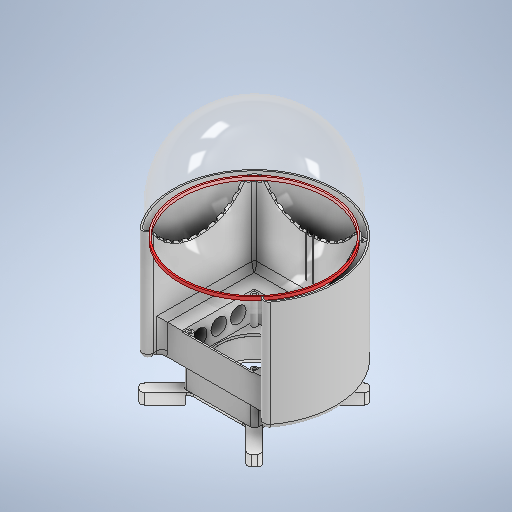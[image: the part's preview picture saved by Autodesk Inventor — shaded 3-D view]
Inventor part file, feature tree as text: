
AUTODESK INVENTOR PART (.ipt)
format: ipt  version: 2025.3 (Build 293356000, 356)  size: 2,002,944 bytes
history: native  units: in
note: dims shown in document units (in); Inventor stores cm internally (conversion verified against a paired STEP export)
features: projected_geometry x27, extrude x22, sketch x21, fillet x10, other x9, pattern_circular x3, mirror x1, helix x1
ambient origin geometry x8: Origin, YZ Plane, XZ Plane, XY Plane, X Axis, Y Axis, Z Axis, Center Point
bodies: Body1 (feature_tree), Body2 (feature_tree), Body3 (feature_tree), Body4 (feature_tree), Body5 (feature_tree), Body6 (feature_tree)
feature tree (94):
  other  "Fan"
  extrude  "Fan Body"  Depth=3.248in
  fillet  "Fillet1"  Radius=0.1772in
  other  "PCB Plane"
  extrude  "PCB extrusion"  Depth=0.1772in
  other  "Bottom of the Coil Plane"
  extrude  "Coil extrusion"  Depth=3.5039in
  sketch  "Sketch5"  dims[d13=0.063in d14=0.0in d15=3.937in]
  other  "Globe revolution"
  extrude  "Inner Wall"  Depth=0.1969in
  sketch  "Sketch7"  dims[d18=0.1575in d19=0.0in d20=7.874in]
  extrude  "Coil Support"  Depth=3.5433in
  extrude  "Coil Support Outer Wall"  Depth=3.937in
  sketch  "Sketch8"  dims[d21=0.0591in d22=90.0deg]
  extrude  "Coil Support Extension"  Depth=0.0787in
  extrude  "Outer Wall"  Depth=7.874in
  extrude  "Extend Walls Bottom of PCB"  TaperAngle=90.0deg  [1 undecoded]
  sketch  "Sketch11"  dims[d27=0.0787in d28=0.0787in d29=0.0in]
  extrude  "Extend Walls to Fan"  Depth=0.1575in TaperAngle=0.0deg
  sketch  "Sketch12"  dims[d30=0.0787in d31=0.0in d34=0.3937in d35=0.0in]
  extrude  "PCB Supports"  Depth=0.0787in TaperAngle=0.0deg
  extrude  "Floor"  Depth=0.3937in TaperAngle=0.0deg
  sketch  "Sketch13"  dims[d36=0.3937in d37=0.0in d40=0.3937in d41=0.0in]
  extrude  "Air Holes"  Depth=0.3937in TaperAngle=0.0deg
  pattern_circular  "Pattern Air Holes"  Count=2  [1 undecoded]
  other  "Cutout Globe"
  extrude  "Cutout Overhang of Coil Support"  Depth=0.7874in
  sketch  "Sketch15"  dims[d50=0.3937in d51=0.0in]
  extrude  "Crown Air Holes"  Depth=0.1181in TaperAngle=0.0deg
  pattern_circular  "Pattern Crown Air Holes"  Count=3  [1 undecoded]
  extrude  "Coil Slots"  Depth=0.3937in TaperAngle=0.0deg
  sketch  "Sketch19"  dims[d62=0.9843in d63=0.1181in d64=0.0in d65=1.1811in d66=-1.2368in]
  sketch  "Sketch20"  dims[d70=90.0deg d71=0.3937in d72=0.0in]
  extrude  "Fill in PCB void"  Depth=0.4331in
  extrude  "PCB Lip"  Depth=3.937in
  extrude  "Repair Fan Air Holes"  Depth=0.1969in TaperAngle=0.0deg
  pattern_circular  "Pattern Repair Air Holes"  Count=3 Angle=180.0deg
  extrude  "Feet Fan Base"  Depth=0.3937in TaperAngle=0.0deg
  extrude  "Feet"  Depth=0.1969in
  mirror  "Feet Mirror"
  fillet  "Feet Fillet 1"  Radius=0.1181in
  fillet  "Feet Fillet 2"  Radius=0.5512in
  extrude  "Extrusion27"  Depth=0.1969in
  fillet  "Fillet4"  Radius=0.3937in
  fillet  "Fillet5"  Radius=7.874in
  fillet  "Fillet6"  Radius=0.1969in
  fillet  "Fillet7"  Radius=0.0787in
  fillet  "Fillet8"  Radius=0.0787in
  fillet  "Fillet11"  Radius=1.5748in
  fillet  "Fillet12"  Radius=0.1969in
  sketch  "Sketch1"  dims[d1=3.622in d2=3.248in d3=0.1772in]
  sketch  "Sketch2"  dims[d4=0.1772in d5=0.1772in]
  other  "PCB"
  sketch  "Sketch4"  dims[d11=1.4567in d12=3.5433in]
  helix  "Coil"  [1 undecoded]
  projected_geometry  "Projected Loop1"
  other  "Globe"
  sketch  "Sketch6"  dims[d16=7.3543in d17=0.0787in]
  projected_geometry  "Projected Loop2"
  other  "Shroud"
  projected_geometry  "Projected Loop3"
  projected_geometry  "Projected Loop4"
  projected_geometry  "Projected Loop6"
  sketch  "Sketch9"  dims[d24=0.0787in d25=0.1575in d26=0.0in]
  projected_geometry  "Projected Loop7"
  sketch  "Sketch14"  dims[d43=0.3937in d44=0.0in]
  projected_geometry  "Projected Loop12"
  projected_geometry  "Projected Loop13"
  projected_geometry  "Projected Loop14"
  projected_geometry  "Projected Loop15"
  sketch  "Sketch17"  dims[d52=0.1181in d53=0.0in d58=0.7874in]
  sketch  "Sketch18"  dims[d59=0.7874in d60=0.7874in d61=0.9843in]
  projected_geometry  "Projected Loop16"
  other  "Foot"
  projected_geometry  "Projected Loop17"
  projected_geometry  "Projected Loop18"
  projected_geometry  "Projected Loop19"
  projected_geometry  "Projected Loop20"
  projected_geometry  "Projected Loop21"
  sketch  "Sketch Circular Pattern2"  dims[d6=0.1772in d7=3.5039in]
  projected_geometry  "Projected Loop23"
  projected_geometry  "Projected Loop24"
  projected_geometry  "Projected Loop25"
  sketch  "Sketch Circular Pattern3"  dims[d8=1.0in d9=0.0in d10=0.1969in]
  projected_geometry  "Projected Loop26"
  projected_geometry  "Projected Loop27"
  projected_geometry  "Projected Loop28"
  projected_geometry  "Projected Loop29"
  projected_geometry  "Projected Loop30"
  sketch  "Sketch21"  dims[d75=0.2756in d76=0.4331in]
  projected_geometry  "Projected Loop31"
  sketch  "Sketch22"  dims[d77=0.7087in d78=3.937in d86=0.1969in d87=0.0in d88=1.1811in d89=180.0deg d91=0.3937in d92=0.0in d93=0.5906in d94=0.1181in d95=0.0in d96=0.5512in d97=0.0in d98=0.1969in d99=0.3937in d100=7.874in d101=0.1969in d102=0.0787in d103=0.0787in d106=1.5748in d108=360.0deg d110=0.1969in d111=7.874in d113=180.0deg d115=0.0197in d116=0.5512in d117=0.0in d118=0.063in d119=0.0in d120=0.063in d121=0.0in d122=1.1811in d123=180.0deg d125=0.3937in d126=0.0in d127=0.1969in d128=0.2756in d129=0.1969in d130=0.2756in d131=0.2756in d134=0.1181in d135=0.2756in d42=0.0197in d45=0.0197in d46=0.0344in d73=0.0197in d74=0.0344in d132=0.0in d133=0.0in]
  projected_geometry  "Projected Loop32"
  projected_geometry  "Projected Loop33"
note: 4 required parameter values undecoded (feature->parameter linkage not recoverable at this tier; creation-order binding heuristic only, values carry confidence <= 0.55)
